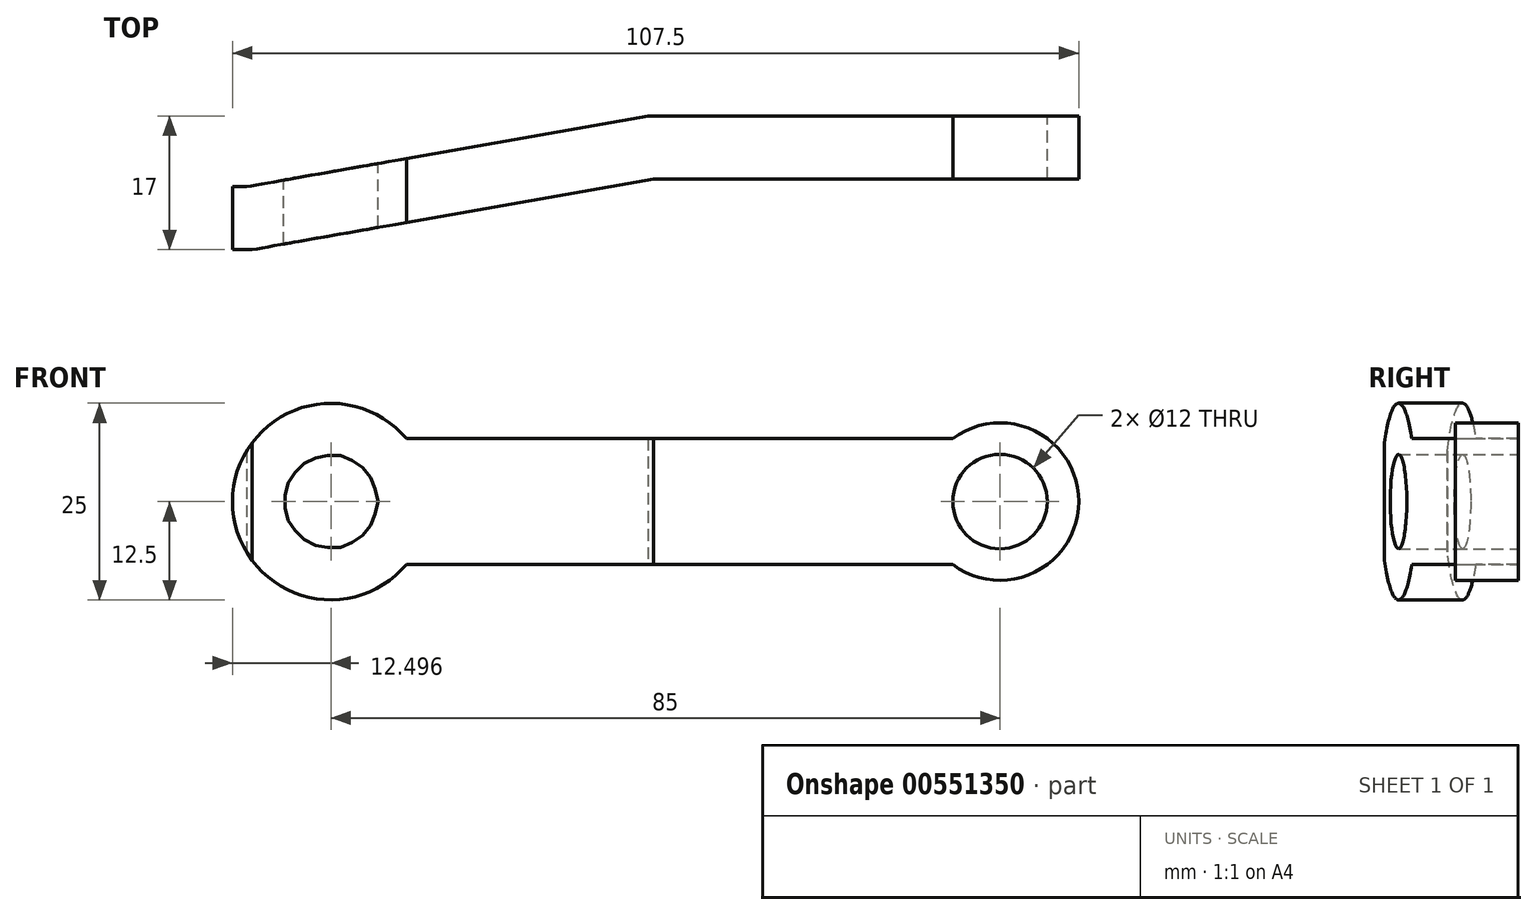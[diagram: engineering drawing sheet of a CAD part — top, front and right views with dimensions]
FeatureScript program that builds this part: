
annotation { "Feature Type Name" : "Feature", "Feature Type Description" : "" }
export const myFeature = defineFeature(function(context is Context, id is Id, definition is map)
    precondition{}
    {
        {
            var Q0;
            Q0=qCreatedBy(makeId("Front.planeOp"),FACE);
            var sketch = newSketch(context, id + "F0", { "sketchPlane" : qUnion([Q0])});
            skCircle(sketch, "E0", {"center": v(-40.31, 0) * mm, "radius": 12.5 * mm});
            skCircle(sketch, "E1", {"center": v(44.69, 0) * mm, "radius": 10 * mm});
            skLineSegment(sketch, "E2", {"start": v(-30.7, 8) * mm, "end": v(38.69, 8) * mm});
            skLineSegment(sketch, "E3.MirrorCS", {"start": v(-30.7, -8) * mm, "end": v(38.69, -8) * mm});
            skCircle(sketch, "E4", {"center": v(-40.31, 0) * mm, "radius": 6 * mm});
            skCircle(sketch, "E5", {"center": v(44.69, 0) * mm, "radius": 6 * mm});
            skSolve(sketch);
        }
        {
            var Q0;
            Q0=makeQuery(id+"F0.imprint","IMPRINT",FACE,{"disambiguationData":[TD([[makeQuery(id+"F0.imprint","IMPRINT",EDGE,{"derivedFrom":sQuery(id+"F0.wireOp",EDGE,"E4")}),-1.0]])]});
            var Q1;
            {var subQ0=sQuery(id+"F0.wireOp",EDGE,"E2");Q1=makeQuery(id+"F0.imprint","IMPRINT",FACE,{"disambiguationData":[TD([[makeQuery(id+"F0.imprint","IMPRINT",EDGE,{"derivedFrom":subQ0}),-1.0]])]});}
            var Q2;
            Q2=makeQuery(id+"F0.imprint","IMPRINT",FACE,{"disambiguationData":[TD([[makeQuery(id+"F0.imprint","IMPRINT",EDGE,{"derivedFrom":sQuery(id+"F0.wireOp",EDGE,"E5")}),-1.0]])]});
            extrude(context, id + "F1", {"entities" : qUnion([Q0, Q1, Q2]), "depth" : 25 * mm, "offsetDistance" : 25 * mm});
        }
        {
            var Q0;
            Q0=qCreatedBy(makeId("Top.planeOp"),FACE);
            var sketch = newSketch(context, id + "F2", { "sketchPlane" : qUnion([Q0])});
            skLineSegment(sketch, "E6", {"start": v(-52.81, -9) * mm, "end": v(-51.04, -9) * mm});
            skLineSegment(sketch, "E7", {"start": v(-51.04, -9) * mm, "end": v(0, 0) * mm});
            skLineSegment(sketch, "E8", {"start": v(25.57, 0) * mm, "end": v(54.69, 0) * mm});
            skLineSegment(sketch, "E9.0", {"start": v(0.7, -8) * mm, "end": v(54.69, -8) * mm});
            skLineSegment(sketch, "E9.1", {"start": v(-50.34, -17) * mm, "end": v(0.7, -8) * mm});
            skLineSegment(sketch, "E9.2", {"start": v(-52.81, -17) * mm, "end": v(-50.34, -17) * mm});
            skPoint(sketch, "E10", {"position": v(45.57, 0) * mm});
            skLineSegment(sketch, "E11", {"start": v(0, 0) * mm, "end": v(25.57, 0) * mm});
            skLineSegment(sketch, "E12", {"start": v(-52.81, -25) * mm, "end": v(-52.81, 0) * mm});
            skLineSegment(sketch, "E13", {"start": v(54.69, 0) * mm, "end": v(54.69, -25) * mm});
            skSolve(sketch);
        }
        {
            var Q0;
            Q0 = qSketchRegion(id + "F2", true);
            extrude(context, id + "F3", {"entities" : qUnion([Q0]), "operationType" : NewBodyOperationType.INTERSECT, "endBound" : BoundingType.SYMMETRIC, "depth" : 25 * mm, "offsetDistance" : 25 * mm});
        }
    });
